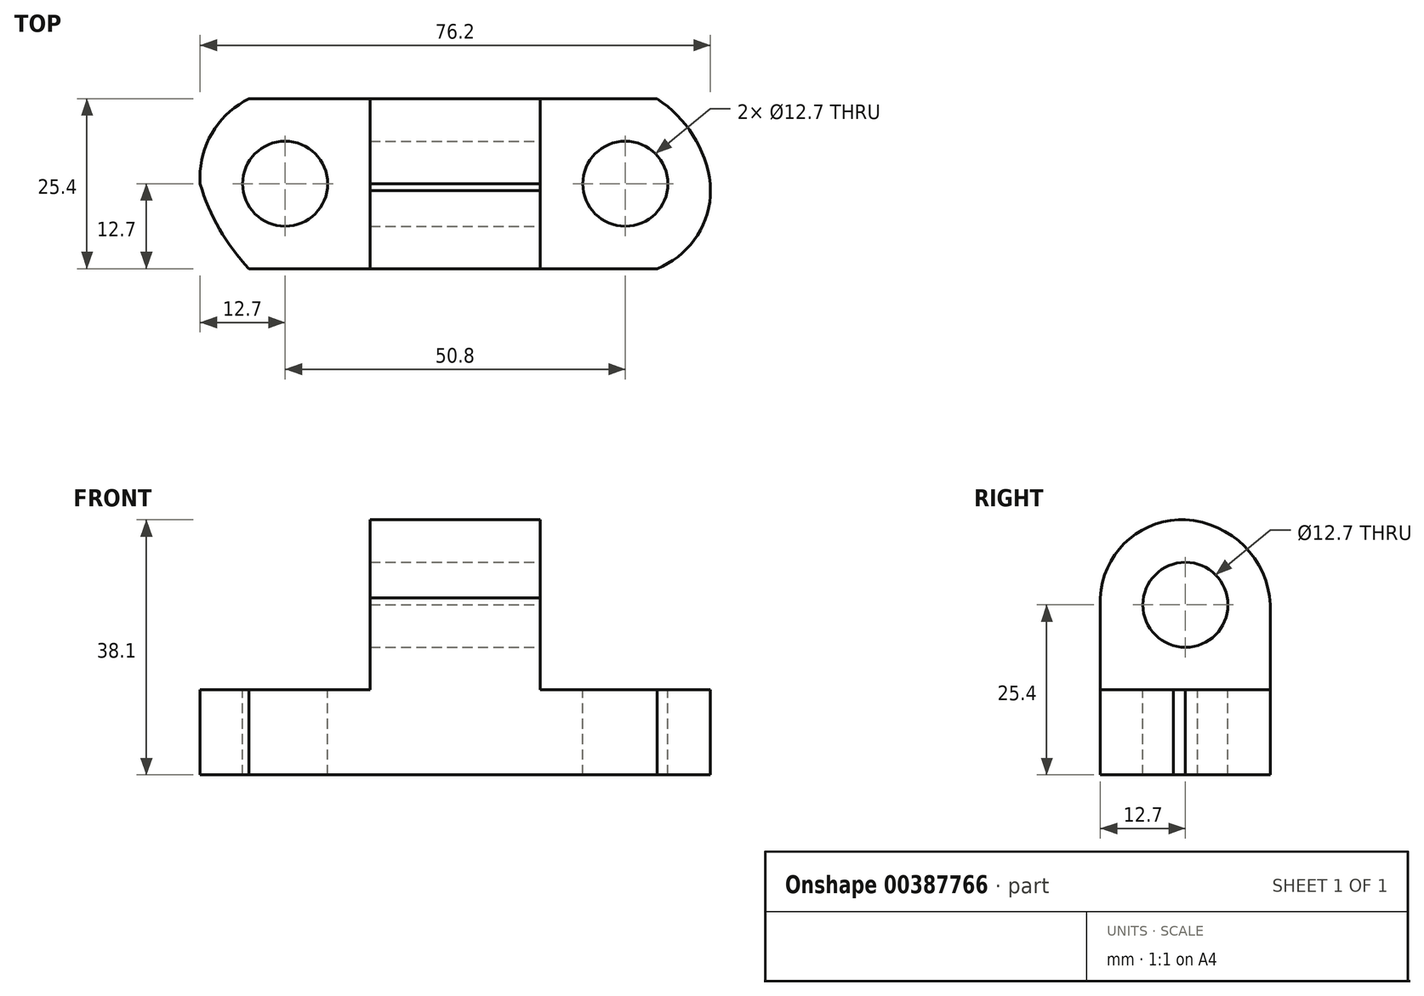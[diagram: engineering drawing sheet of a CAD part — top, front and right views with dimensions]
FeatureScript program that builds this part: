
annotation { "Feature Type Name" : "Feature", "Feature Type Description" : "" }
export const myFeature = defineFeature(function(context is Context, id is Id, definition is map)
    precondition{}
    {
        {
            var Q0;
            Q0=qCreatedBy(makeId("Front.planeOp"),FACE);
            var sketch = newSketch(context, id + "F0", { "sketchPlane" : qUnion([Q0])});
            skLineSegment(sketch, "E0", {"start": v(0, 0) * mm, "end": v(0, 12.7) * mm});
            skLineSegment(sketch, "E1", {"start": v(0, 12.7) * mm, "end": v(25.4, 12.7) * mm});
            skLineSegment(sketch, "E2", {"start": v(25.4, 12.7) * mm, "end": v(25.4, 38.1) * mm});
            skLineSegment(sketch, "E3", {"start": v(25.4, 38.1) * mm, "end": v(50.8, 38.1) * mm});
            skLineSegment(sketch, "E4", {"start": v(50.8, 38.1) * mm, "end": v(50.8, 12.7) * mm});
            skLineSegment(sketch, "E5", {"start": v(50.8, 12.7) * mm, "end": v(76.2, 12.7) * mm});
            skLineSegment(sketch, "E6", {"start": v(76.2, 12.7) * mm, "end": v(76.2, 0) * mm});
            skLineSegment(sketch, "E7", {"start": v(76.2, 0) * mm, "end": v(0, 0) * mm});
            skSolve(sketch);
        }
        {
            var Q0;
            Q0 = qSketchRegion(id + "F0", true);
            extrude(context, id + "F1", {"entities" : qUnion([Q0]), "depth" : 25.4 * mm});
        }
        {
            var Q0;
            Q0=makeQuery(id+"F1.opExtrude","SWEPT_FACE",FACE,{"disambiguationData":[OSD([sQuery(id+"F0.wireOp",EDGE,"E5")])]});
            var sketch = newSketch(context, id + "F2", { "sketchPlane" : qUnion([Q0])});
            skCircle(sketch, "E8", {"center": v(63.5, -12.7) * mm, "radius": 6.35 * mm});
            skPoint(sketch, "E8.centerSnap0", {"position": v(63.5, 0) * mm});
            skSolve(sketch);
        }
        {
            var Q0;
            Q0=makeQuery(id+"F2.imprint","IMPRINT",FACE,{"disambiguationData":[TD([[makeQuery(id+"F2.imprint","IMPRINT",EDGE,{"derivedFrom":sQuery(id+"F2.wireOp",EDGE,"E8")}),1.0]])]});
            extrude(context, id + "F3", {"entities" : qUnion([Q0]), "operationType" : NewBodyOperationType.REMOVE, "oppositeDirection" : true, "depth" : 25.4 * mm});
        }
        {
            var Q0;
            Q0=makeQuery(id+"F1.opExtrude","SWEPT_FACE",FACE,{"disambiguationData":[OSD([sQuery(id+"F0.wireOp",EDGE,"E1")])]});
            var sketch = newSketch(context, id + "F4", { "sketchPlane" : qUnion([Q0])});
            skCircle(sketch, "E9", {"center": v(12.7, -12.7) * mm, "radius": 6.35 * mm});
            skPoint(sketch, "E9.centerSnap0", {"position": v(12.7, -25.4) * mm});
            skSolve(sketch);
        }
        {
            var Q0;
            Q0=makeQuery(id+"F4.imprint","IMPRINT",FACE,{"disambiguationData":[TD([[makeQuery(id+"F4.imprint","IMPRINT",EDGE,{"derivedFrom":sQuery(id+"F4.wireOp",EDGE,"E9")}),1.0]])]});
            extrude(context, id + "F5", {"entities" : qUnion([Q0]), "operationType" : NewBodyOperationType.REMOVE, "oppositeDirection" : true, "depth" : 25.4 * mm});
        }
        {
            var Q0;
            Q0=makeQuery(id+"F1.opExtrude","SWEPT_FACE",FACE,{"disambiguationData":[OSD([sQuery(id+"F0.wireOp",EDGE,"E4")])]});
            var sketch = newSketch(context, id + "F6", { "sketchPlane" : qUnion([Q0])});
            skCircle(sketch, "E10", {"center": v(-12.7, 25.4) * mm, "radius": 6.35 * mm});
            skPoint(sketch, "E10.centerSnap0", {"position": v(-12.7, 38.1) * mm});
            skSolve(sketch);
        }
        {
            var Q0;
            Q0=makeQuery(id+"F6.imprint","IMPRINT",FACE,{"disambiguationData":[TD([[makeQuery(id+"F6.imprint","IMPRINT",EDGE,{"derivedFrom":sQuery(id+"F6.wireOp",EDGE,"E10")}),1.0]])]});
            extrude(context, id + "F7", {"entities" : qUnion([Q0]), "operationType" : NewBodyOperationType.REMOVE, "oppositeDirection" : true, "depth" : 25.4 * mm});
        }
        {
            var Q0;
            Q0=makeQuery(id+"F1.opExtrude","SWEPT_FACE",FACE,{"disambiguationData":[OSD([sQuery(id+"F0.wireOp",EDGE,"E5")])]});
            var sketch = newSketch(context, id + "F8", { "sketchPlane" : qUnion([Q0])});
            skArc(sketch, "E11", {"start": v(68.24, -25.4) * mm, "mid": v(74.3, -20.35) * mm, "end": v(76.2, -12.7) * mm});
            skArc(sketch, "E12", {"start": v(76.2, -12.7) * mm, "mid": v(73.61, -5.48) * mm, "end": v(68.24, 0) * mm});
            skSolve(sketch);
        }
        {
            var Q0;
            Q0 = qSketchRegion(id + "F8", true);
            var Q1;
            {var subQ0=sQuery(id+"F8.wireOp",EDGE,"E12");Q1=makeQuery(id+"F8.imprint","IMPRINT",FACE,{"disambiguationData":[TD([[makeQuery(id+"F8.imprint","IMPRINT",EDGE,{"derivedFrom":subQ0}),-1.0]])]});}
            var Q2;
            {var subQ0=sQuery(id+"F8.wireOp",EDGE,"E11");var subQ1=sQuery(id+"F0.wireOp",EDGE,"E5");var subQ2=makeQuery(id+"F1.opExtrude","CAP_EDGE",EDGE,{"disambiguationData":[OSD([subQ1])],"isStart":false});var subQ3=makeQuery(id+"F8.imprint","INTERSECT",VERTEX,{"derivedFrom":[subQ2,subQ0]});Q2=makeQuery(id+"F8.imprint","IMPRINT",FACE,{"disambiguationData":[TD([[makeQuery(id+"F8.imprint","IMPRINT",EDGE,{"disambiguationData":[TD([[subQ3,-1.0]])],"derivedFrom":subQ0}),-1.0]])]});}
            extrude(context, id + "F9", {"entities" : qUnion([Q0, Q1, Q2]), "operationType" : NewBodyOperationType.REMOVE, "oppositeDirection" : true, "depth" : 25.4 * mm});
        }
        {
            var Q0;
            Q0=makeQuery(id+"F1.opExtrude","SWEPT_FACE",FACE,{"disambiguationData":[OSD([sQuery(id+"F0.wireOp",EDGE,"E1")])]});
            var sketch = newSketch(context, id + "F10", { "sketchPlane" : qUnion([Q0])});
            skArc(sketch, "E13", {"start": v(7.31, 0) * mm, "mid": v(1.72, -5.24) * mm, "end": v(0, -12.7) * mm});
            skArc(sketch, "E14", {"start": v(0, -12.7) * mm, "mid": v(2.9, -19.48) * mm, "end": v(7.31, -25.4) * mm});
            skSolve(sketch);
        }
        {
            var Q0;
            Q0 = qSketchRegion(id + "F10", true);
            var Q1;
            {var subQ0=sQuery(id+"F10.wireOp",EDGE,"E13");var subQ1=sQuery(id+"F0.wireOp",EDGE,"E1");var subQ2=makeQuery(id+"F1.opExtrude","CAP_EDGE",EDGE,{"disambiguationData":[OSD([subQ1])],"isStart":true});var subQ3=makeQuery(id+"F10.imprint","INTERSECT",VERTEX,{"derivedFrom":[subQ2,subQ0]});Q1=makeQuery(id+"F10.imprint","IMPRINT",FACE,{"disambiguationData":[TD([[makeQuery(id+"F10.imprint","IMPRINT",EDGE,{"disambiguationData":[TD([[subQ3,-1.0]])],"derivedFrom":subQ0}),-1.0]])]});}
            var Q2;
            {var subQ0=sQuery(id+"F10.wireOp",EDGE,"E14");Q2=makeQuery(id+"F10.imprint","IMPRINT",FACE,{"disambiguationData":[TD([[makeQuery(id+"F10.imprint","IMPRINT",EDGE,{"derivedFrom":subQ0}),-1.0]])]});}
            extrude(context, id + "F11", {"entities" : qUnion([Q0, Q1, Q2]), "operationType" : NewBodyOperationType.REMOVE, "oppositeDirection" : true, "depth" : 25.4 * mm});
        }
        {
            var Q0;
            Q0=makeQuery(id+"F1.opExtrude","SWEPT_FACE",FACE,{"disambiguationData":[OSD([sQuery(id+"F0.wireOp",EDGE,"E4")])]});
            var sketch = newSketch(context, id + "F12", { "sketchPlane" : qUnion([Q0])});
            skArc(sketch, "E15", {"start": v(-12.7, 38.1) * mm, "mid": v(-21.84, 34.54) * mm, "end": v(-25.4, 25.4) * mm});
            skArc(sketch, "E16", {"start": v(0, 25.4) * mm, "mid": v(-3.92, 34.18) * mm, "end": v(-12.7, 38.1) * mm});
            skSolve(sketch);
        }
        {
            var Q0;
            {var subQ0=sQuery(id+"F12.wireOp",EDGE,"E16");Q0=makeQuery(id+"F12.imprint","IMPRINT",FACE,{"disambiguationData":[TD([[makeQuery(id+"F12.imprint","IMPRINT",EDGE,{"derivedFrom":subQ0}),-1.0]])]});}
            var Q1;
            {var subQ0=sQuery(id+"F12.wireOp",EDGE,"E15");var subQ1=sQuery(id+"F0.wireOp",EDGE,"E4");var subQ4=makeQuery(id+"F1.opExtrude","CAP_EDGE",EDGE,{"disambiguationData":[OSD([subQ1])],"isStart":false});var subQ5=makeQuery(id+"F12.imprint","INTERSECT",VERTEX,{"disambiguationData":[OD(1.0)],"derivedFrom":[subQ4,subQ0]});Q1=makeQuery(id+"F12.imprint","IMPRINT",FACE,{"disambiguationData":[TD([[makeQuery(id+"F12.imprint","IMPRINT",EDGE,{"disambiguationData":[TD([[subQ5,1.0]])],"derivedFrom":subQ0}),-1.0]])]});}
            extrude(context, id + "F13", {"entities" : qUnion([Q0, Q1]), "operationType" : NewBodyOperationType.REMOVE, "oppositeDirection" : true, "depth" : 25.4 * mm});
        }
    });
